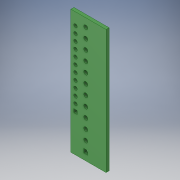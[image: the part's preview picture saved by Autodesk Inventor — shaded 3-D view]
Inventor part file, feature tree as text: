
AUTODESK INVENTOR PART (.ipt)
format: ipt  version: 2018 (Build 220112000, 112)  size: 2,886,656 bytes
history: native  units: in
note: dims shown in document units (in); Inventor stores cm internally (conversion verified against a paired STEP export)
features: sketch x2, extrude x1
ambient origin geometry x8: Origin, YZ Plane, XZ Plane, XY Plane, X Axis, Y Axis, Z Axis, Center Point
bodies: Body1 (feature_tree)
feature tree (3):
  sketch  "Sketch13"
  extrude  "Extrusion4"  [1 undecoded]
  sketch  "Sketch5"  dims[d6=0.062in d7=0.0in]
note: 1 required parameter value undecoded (feature->parameter linkage not recoverable at this tier; creation-order binding heuristic only, values carry confidence <= 0.55)
